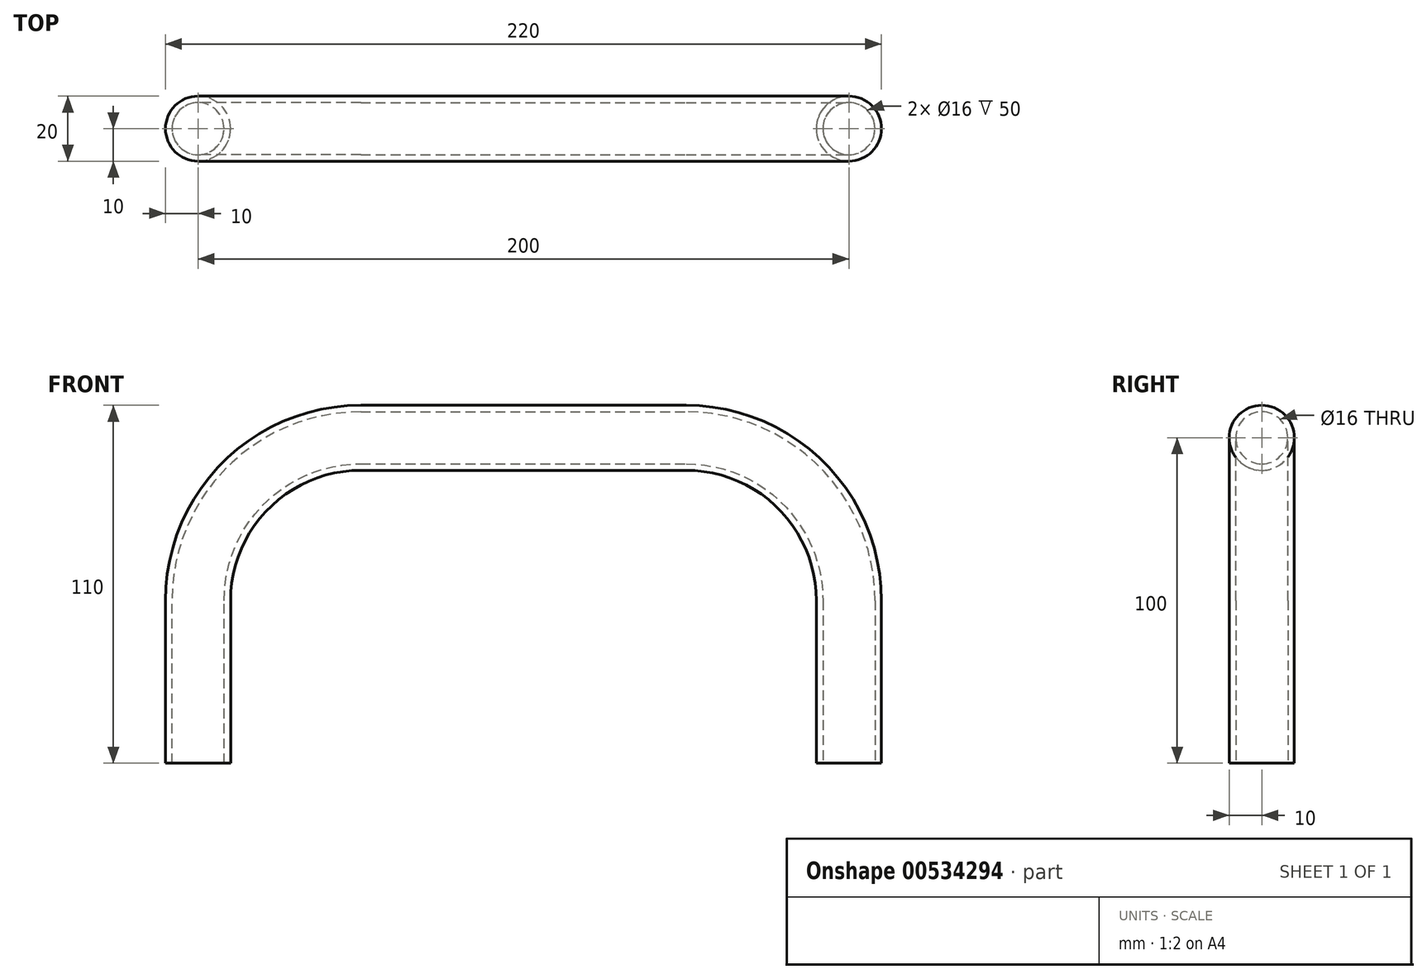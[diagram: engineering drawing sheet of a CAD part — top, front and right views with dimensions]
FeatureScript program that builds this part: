
annotation { "Feature Type Name" : "Feature", "Feature Type Description" : "" }
export const myFeature = defineFeature(function(context is Context, id is Id, definition is map)
    precondition{}
    {
        {
            var Q0;
            Q0=qCreatedBy(makeId("Top.planeOp"),FACE);
            var sketch = newSketch(context, id + "F0", { "sketchPlane" : qUnion([Q0])});
            skCircle(sketch, "E0", {"center": v(0, 0) * mm, "radius": 10 * mm});
            skCircle(sketch, "E1", {"center": v(0, 0) * mm, "radius": 8 * mm});
            skSolve(sketch);
        }
        {
            var Q0;
            Q0=qCreatedBy(makeId("Front.planeOp"),FACE);
            var sketch = newSketch(context, id + "F1", { "sketchPlane" : qUnion([Q0])});
            skLineSegment(sketch, "E2", {"start": v(0, 0) * mm, "end": v(0, 50) * mm});
            skLineSegment(sketch, "E3", {"start": v(50, 100) * mm, "end": v(150, 100) * mm});
            skLineSegment(sketch, "E4", {"start": v(200, 50) * mm, "end": v(200, 0) * mm});
            skPoint(sketch, "E5.visualSharp", {"position": v(0, 100) * mm});
            skArc(sketch, "E5.filletArc", {"start": v(50, 100) * mm, "mid": v(14.64, 85.36) * mm, "end": v(0, 50) * mm});
            skPoint(sketch, "E6.visualSharp", {"position": v(200, 100) * mm});
            skArc(sketch, "E6.filletArc", {"start": v(200, 50) * mm, "mid": v(185.36, 85.36) * mm, "end": v(150, 100) * mm});
            skSolve(sketch);
        }
        {
            var Q0;
            Q0=makeQuery(id+"F0.imprint","IMPRINT",FACE,{"disambiguationData":[TD([[makeQuery(id+"F0.imprint","IMPRINT",EDGE,{"derivedFrom":sQuery(id+"F0.wireOp",EDGE,"E0")}),1.0]])]});
            var Q1;
            Q1=sQuery(id+"F1.wireOp",EDGE,"E2");
            var Q2;
            Q2=sQuery(id+"F1.wireOp",EDGE,"E5.filletArc");
            var Q3;
            Q3=sQuery(id+"F1.wireOp",EDGE,"E3");
            var Q4;
            Q4=sQuery(id+"F1.wireOp",EDGE,"E6.filletArc");
            var Q5;
            Q5=sQuery(id+"F1.wireOp",EDGE,"E4");
            sweep(context, id + "F2", {"profiles" : qUnion([Q0]), "path" : qUnion([Q1, Q2, Q3, Q4, Q5])});
        }
    });
